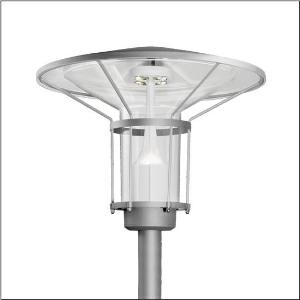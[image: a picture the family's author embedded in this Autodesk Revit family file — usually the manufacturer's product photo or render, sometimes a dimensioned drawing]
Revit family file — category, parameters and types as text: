
# Revit family: laterne_classic_iq___p1_0a_5xa5245nf14h_cdb6
name_source: partatom
category: Lighting Fixtures
units: mm (PartAtom-declared; Revit-internal decimal feet)

## family parameters
Cut with Voids When Loaded = No
Host = Face
Light Source = No
Part Type = Normal
Room Calculation Point = No
Round Connector Dimension = Use Diameter
Shared = No

## types (1)
- --- (1 x LED, 1360 lm, 11.8 W, 2700K)
    Apparent Load = 12 VA
    CIE Flux Codes = 30 61 91 96 100
    Color Rendering = 70
    Color Temperature = 2700K
    Default Elevation = 1800 mm
    Description = Lantern Classic iQ, mast luminaire, Module 540 iQ-SR, primary light control with 3 zone facetted reflector, of plastic, silver coated, highly specular, structured, primary optical cover: cover, of PMMA, transparent, light distribution: P1.0a, light emission: direct distribution, primary light characteristic: strongly asymmetric, installation type: post-top, LED, High Power LED, rated luminous flux: 1.360lm, luminous efficacy: 115lm/W, light colour: 727, colour temperature: 2700K, control gear: ECG iQ, control: presetting dimming logarithmic, Street-Remote, Auto-Match, Temp-Guard, Lumen-Switch, Night-Set, Smart-Wire, Light-Fading, Desk-Remote (wireless, voltage-free reading and setting of iQ features in the workshop via application-optimized NFC function/RFID function), optimised constant luminous flux control (CLO 2.0), with terminal, 6-pole, max. 2.5mm², mains connection: 230..240V, AC, 50/60Hz, start of lifetime: 12W, end of service life: 12W, reduction: 5W, luminaire housing, upper part, of glass-fibre reinforced polyester, coated, Siteco® metallic grey (DB 702S), diameter: 750mm, height: 596mm, spigot size: d x l = 76 x 70mm (post-top) | with reducer (optional accessory) 60 x 70mm, post-top mast mounting element, of diecast aluminium, coated, Siteco® metallic grey (DB 702S), Module 540 iQ-SR, traffic white (RAL 9016), equipment: standard, protection rating (complete): IP65, insulation class (complete): insulation class II (safety insulation), certification: CE, ENEC, VDE, packaging unit: 1 piece

Light Distribution: P1.0a
    Height = 596 mm
    Lamp = 1 x LED
    Lamp Light Flux = 1360 lm
    Lamp Power = 11.8 W
    Lamp count = 1
    Length = 750 mm
    Luminous efficacy = 115 lm/W
    Manufacturer = Siteco
    ModVariant = No
    Model = 5XA5245NF14H
    Number of Poles = 1
    OnlyDefault = Yes
    Power Factor = 1
    Product Name = Laterne Classic iQ | P1.0a
    Product group = mast luminaire | pylon top
    ProductGroupID = 6100
    Protection Class = Protection class II
    Protection Degree = IP 65
    RLX_Detail_Level = 1
    RLX_Emergency_Light_Flux = 0 lm
    RLX_Emergency_Type = 0
    RLX_Emergency_Type_DB = No
    RlxData = <blob elided: 93905 chars, md5=ae08d97b>
    Socket = socket
    Standby Power = 0 W
    System Light Flux = 1360 lm
    System Power = 12 W
    Type Comments = factory setting: luminous flux: 100 % | dim-lin: 254 | 472 mA
    Type Image = l_1006052.jpg
    URL = http://relux.com
    VarID = @adj_103467
    Voltage = 0 V
    Weight = 0.00 kg
    Width = 0 mm  [stored 0 ft]

note: [stored X ft] marks values corroborated as IEEE doubles in the binary element streams (Revit-internal decimal feet)

## geometry (parser evidence)
native form markers: Blend x4, Sweep x10
no freeform markers — native parametric forms only
